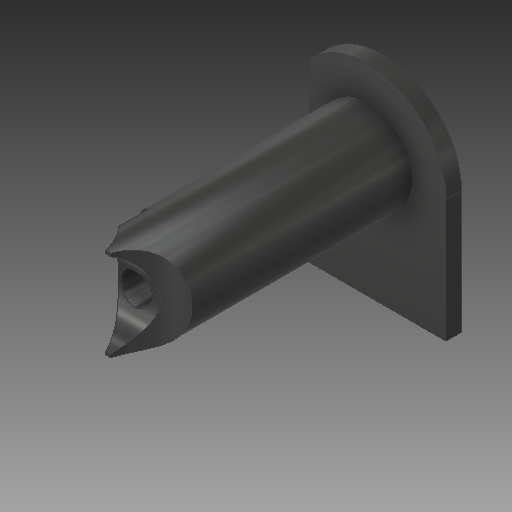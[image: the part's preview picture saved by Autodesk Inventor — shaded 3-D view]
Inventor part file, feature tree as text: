
AUTODESK INVENTOR PART (.ipt)
format: ipt  version: 2018 (Build 220112000, 112)  size: 194,048 bytes
history: native  units: in
note: dims shown in document units (in); Inventor stores cm internally (conversion verified against a paired STEP export)
features: extrude x7, sketch x7, chamfer x1
ambient origin geometry x8: Origin, YZ Plane, XZ Plane, XY Plane, X Axis, Y Axis, Z Axis, Center Point
bodies: Solid1 (feature_tree)
feature tree (15):
  extrude  "Extrusion1"  Depth=0.8661in TaperAngle=0.0deg
  extrude  "Extrusion2"  Depth=0.1811in
  extrude  "Extrusion3"  Depth=0.0492in TaperAngle=0.0deg
  extrude  "Extrusion4"  Depth=0.6299in TaperAngle=0.0deg
  chamfer  "Chamfer1"  Distance=0.6299in
  extrude  "Extrusion5"  Depth=0.2136in
  extrude  "Extrusion6"  TaperAngle=0.0deg  [1 undecoded]
  extrude  "Extrusion7"  TaperAngle=30.0deg  [1 undecoded]
  sketch  "Sketch1"  dims[d0=0.2854in d1=0.8661in d2=0.0in]
  sketch  "Sketch2"  dims[d3=0.248in d4=0.1811in]
  sketch  "Sketch3"  dims[d5=0.3858in d6=0.0492in d7=0.0in]
  sketch  "Sketch4"  dims[d8=0.1732in d9=0.6299in d10=0.0in]
  sketch  "Sketch5"  dims[d11=0.0984in d12=0.6299in d13=0.0in]
  sketch  "Sketch6"  dims[d14=0.0551in d15=0.0787in d16=45.0deg d17=0.2136in]
  sketch  "Sketch7"  dims[d18=0.6693in d19=0.0in d20=0.0in d21=30.0deg d22=0.1811in d23=0.2126in d24=0.0551in d25=0.0in d26=0.0in d27=0.6299in d28=0.0in d29=0.0118in]
note: 2 required parameter values undecoded (feature->parameter linkage not recoverable at this tier; creation-order binding heuristic only, values carry confidence <= 0.55)
